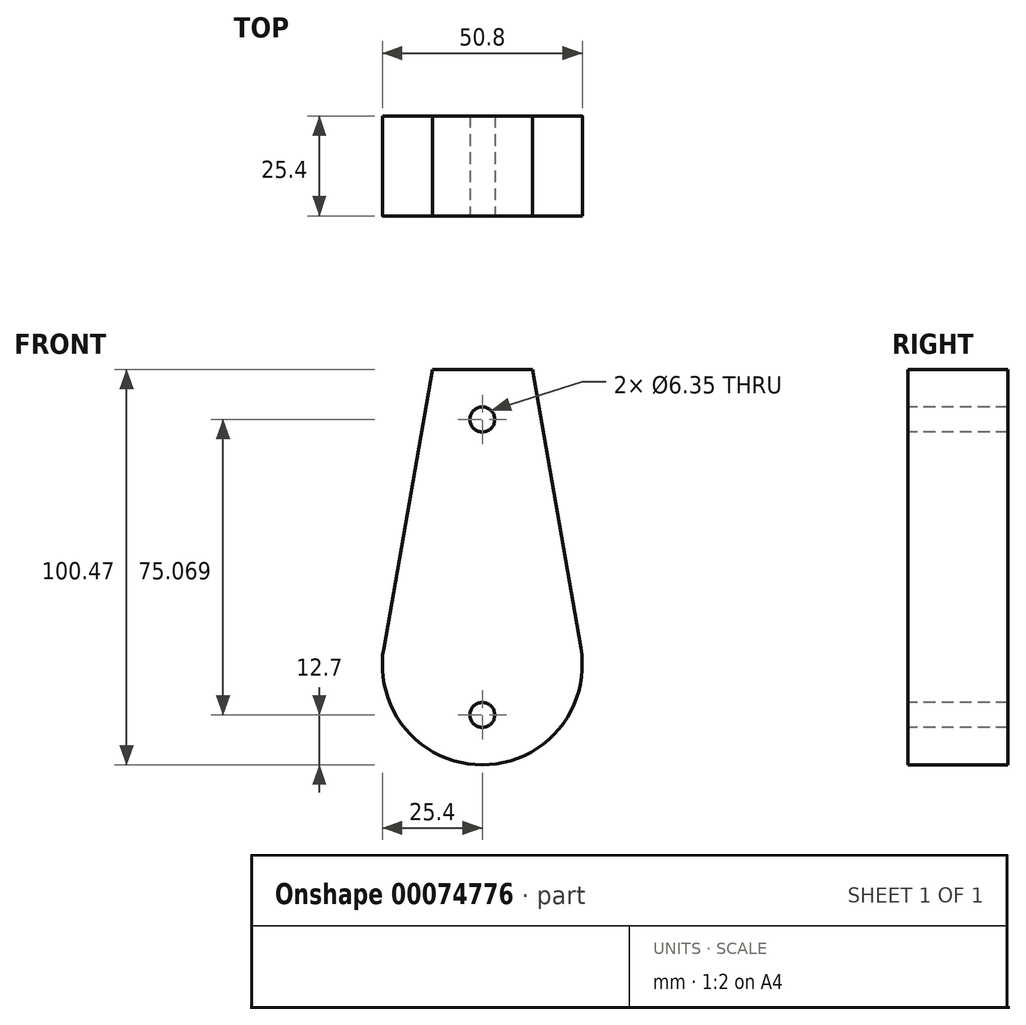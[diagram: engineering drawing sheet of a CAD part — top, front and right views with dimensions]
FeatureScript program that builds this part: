
annotation { "Feature Type Name" : "Feature", "Feature Type Description" : "" }
export const myFeature = defineFeature(function(context is Context, id is Id, definition is map)
    precondition{}
    {
        {
            var Q0;
            Q0=qCreatedBy(makeId("Front.planeOp"),FACE);
            var sketch = newSketch(context, id + "F0", { "sketchPlane" : qUnion([Q0])});
            skArc(sketch, "E0", {"start": v(-25.02, 4.36) * mm, "mid": v(0, -25.4) * mm, "end": v(25.02, 4.36) * mm});
            skLineSegment(sketch, "E1", {"start": v(-12.7, 75.07) * mm, "end": v(12.7, 75.07) * mm});
            skLineSegment(sketch, "E2", {"start": v(12.7, 75.07) * mm, "end": v(25.78, 0) * mm});
            skLineSegment(sketch, "E3", {"start": v(25.78, 0) * mm, "end": v(25.4, 0) * mm});
            skLineSegment(sketch, "E4", {"start": v(-12.7, 75.07) * mm, "end": v(-25.78, 0) * mm});
            skPoint(sketch, "E5.trimOffspring.end.orphan", {"position": v(-25.4, 0) * mm});
            skPoint(sketch, "E6.positionSnap0", {"position": v(0, 75.07) * mm});
            skSolve(sketch);
        }
        {
            var Q0;
            {var subQ3=sQuery(id+"F0.wireOp",EDGE,"E1");Q0=makeQuery(id+"F0.imprint","IMPRINT",FACE,{"disambiguationData":[TD([[makeQuery(id+"F0.imprint","IMPRINT",EDGE,{"derivedFrom":subQ3}),-1.0]])]});}
            extrude(context, id + "F1", {"entities" : qUnion([Q0]), "oppositeDirection" : true, "depth" : 25.4 * mm});
        }
        {
            var Q0;
            Q0=qCreatedBy(makeId("Front.planeOp"),FACE);
            var sketch = newSketch(context, id + "F2", { "sketchPlane" : qUnion([Q0])});
            skPoint(sketch, "E7", {"position": v(0, -12.7) * mm});
            skPoint(sketch, "E8", {"position": v(0, 62.37) * mm});
            skSolve(sketch);
        }
        {
            var Q0;
            Q0=sQuery(id+"F2.wireOp",VERTEX,"E7");
            var Q1;
            Q1=sQuery(id+"F2.wireOp",VERTEX,"E8");
            var Q2;
            Q2=makeQuery(id+"F1.opExtrude","SWEPT_BODY",BODY,{"disambiguationData":[OSD([sQuery(id+"F0.wireOp",EDGE,"E0"),sQuery(id+"F0.wireOp",EDGE,"E1"),sQuery(id+"F0.wireOp",EDGE,"E2"),sQuery(id+"F0.wireOp",EDGE,"E4")])]});
            hole(context, id + "F3", {"style" : HoleStyle.SIMPLE, "holeDiameter" : 6.35 * mm, "endStyle" : HoleEndStyle.THROUGH, "locations" : qUnion([Q0, Q1]), "scope" : qUnion([Q2])});
        }
    });
